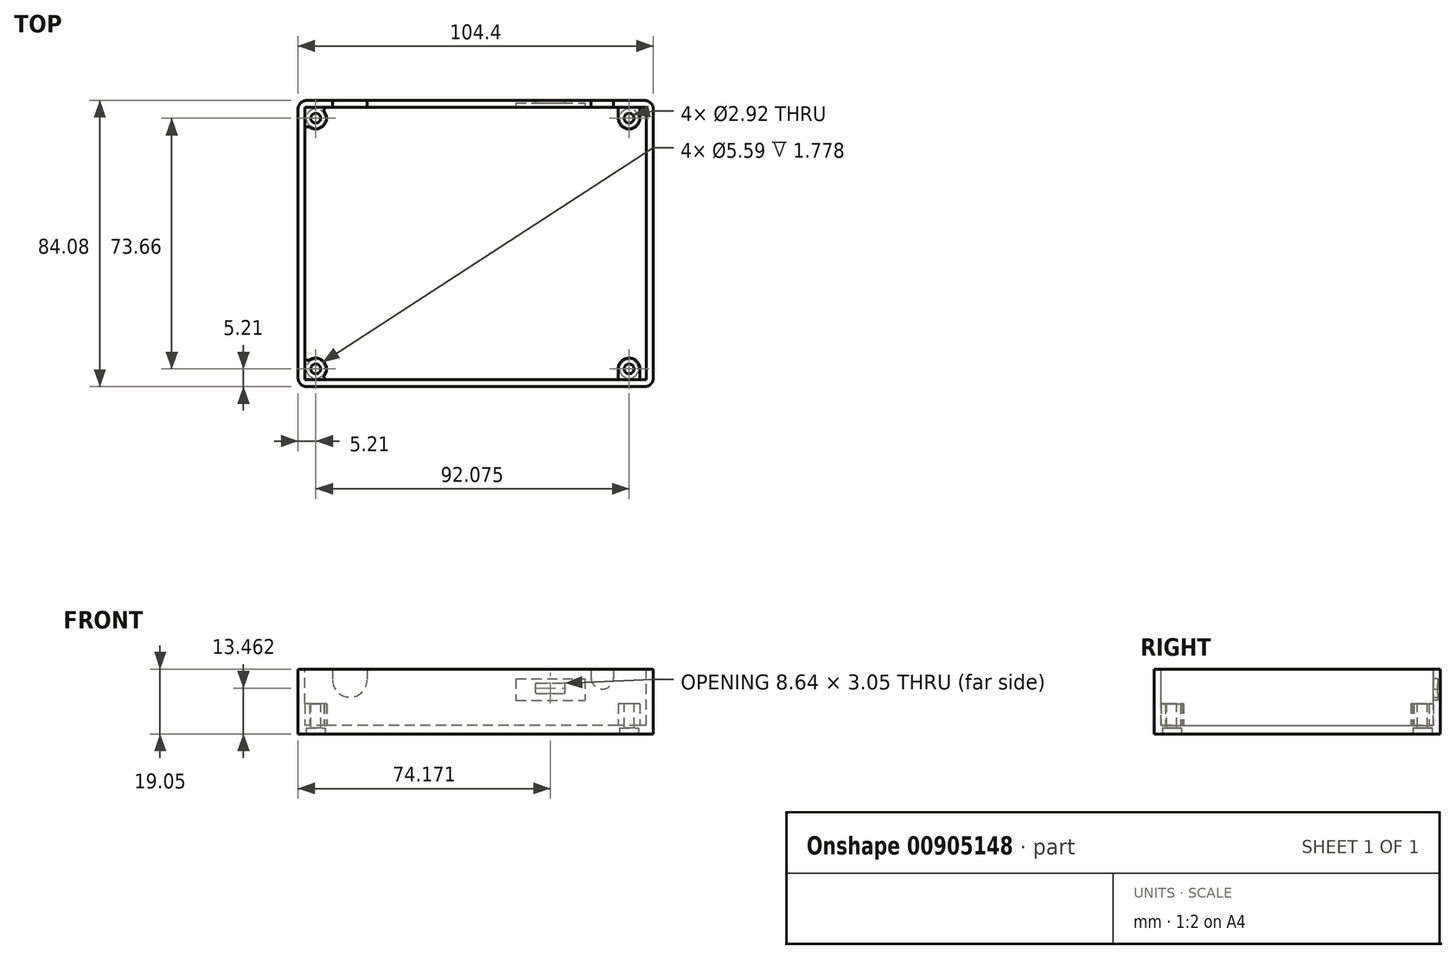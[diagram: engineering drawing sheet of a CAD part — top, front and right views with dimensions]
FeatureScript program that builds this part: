
annotation { "Feature Type Name" : "Feature", "Feature Type Description" : "" }
export const myFeature = defineFeature(function(context is Context, id is Id, definition is map)
    precondition{}
    {
        {
            var Q0;
            Q0=qCreatedBy(makeId("Top.planeOp"),FACE);
            var sketch = newSketch(context, id + "F0", { "sketchPlane" : qUnion([Q0])});
            skLineSegment(sketch, "E0.bottom", {"start": v(52.2, -42.04) * mm, "end": v(-52.2, -42.04) * mm});
            skLineSegment(sketch, "E0.top", {"start": v(52.2, 42.04) * mm, "end": v(-52.2, 42.04) * mm});
            skLineSegment(sketch, "E0.left", {"start": v(52.2, -42.04) * mm, "end": v(52.2, 42.04) * mm});
            skLineSegment(sketch, "E0.right", {"start": v(-52.2, -42.04) * mm, "end": v(-52.2, 42.04) * mm});
            skPoint(sketch, "E0.middle", {"position": v(0, 0) * mm});
            skSolve(sketch);
        }
        {
            var Q0;
            Q0 = qSketchRegion(id + "F0", true);
            extrude(context, id + "F1", {"entities" : qUnion([Q0]), "depth" : 19.05 * mm, "offsetDistance" : 25.4 * mm});
        }
        {
            var Q0;
            Q0=makeQuery(id+"F1.opExtrude","CAP_FACE",FACE,{"disambiguationData":[OSD([sQuery(id+"F0.wireOp",EDGE,"E0.bottom"),sQuery(id+"F0.wireOp",EDGE,"E0.top"),sQuery(id+"F0.wireOp",EDGE,"E0.left"),sQuery(id+"F0.wireOp",EDGE,"E0.right")])],"isStart":false});
            var sketch = newSketch(context, id + "F2", { "sketchPlane" : qUnion([Q0])});
            skLineSegment(sketch, "E1.bottom", {"start": v(50.16, -40) * mm, "end": v(-50.16, -40) * mm});
            skLineSegment(sketch, "E1.top", {"start": v(50.16, 40) * mm, "end": v(-50.16, 40) * mm});
            skLineSegment(sketch, "E1.left", {"start": v(50.16, -40) * mm, "end": v(50.16, 40) * mm});
            skLineSegment(sketch, "E1.right", {"start": v(-50.16, -40) * mm, "end": v(-50.16, 40) * mm});
            skPoint(sketch, "E1.middle", {"position": v(0, 0) * mm});
            skSolve(sketch);
        }
        {
            var Q0;
            Q0=makeQuery(id+"F2.imprint","IMPRINT",FACE,{"disambiguationData":[TD([[makeQuery(id+"F2.imprint","IMPRINT",EDGE,{"derivedFrom":sQuery(id+"F2.wireOp",EDGE,"E1.bottom")}),-1.0]])]});
            extrude(context, id + "F3", {"entities" : qUnion([Q0]), "operationType" : NewBodyOperationType.REMOVE, "oppositeDirection" : true, "depth" : 16.5 * mm, "offsetDistance" : 25.4 * mm});
        }
        {
            var Q0;
            Q0=makeQuery(id+"F1.opExtrude","SWEPT_FACE",FACE,{"disambiguationData":[OSD([sQuery(id+"F0.wireOp",EDGE,"E0.top")])]});
            var sketch = newSketch(context, id + "F4", { "sketchPlane" : qUnion([Q0])});
            skPoint(sketch, "E2", {"position": v(36.96, 15.88) * mm});
            skCircle(sketch, "E3", {"center": v(36.96, 15.88) * mm, "radius": 5.08 * mm});
            skLineSegment(sketch, "E4", {"start": v(36.96, 15.88) * mm, "end": v(31.88, 15.88) * mm, "construction": true});
            skLineSegment(sketch, "E5", {"start": v(36.96, 15.88) * mm, "end": v(42.04, 15.88) * mm, "construction": true});
            skLineSegment(sketch, "E6", {"start": v(31.88, 15.88) * mm, "end": v(31.88, 19.05) * mm});
            skLineSegment(sketch, "E7", {"start": v(42.04, 15.88) * mm, "end": v(42.04, 19.05) * mm});
            skSolve(sketch);
        }
        {
            var Q0;
            Q0 = qSketchRegion(id + "F4", true);
            var Q1;
            {var subQ0=sQuery(id+"F4.wireOp",EDGE,"E7");Q1=makeQuery(id+"F4.imprint","IMPRINT",FACE,{"disambiguationData":[TD([[makeQuery(id+"F4.imprint","IMPRINT",EDGE,{"derivedFrom":subQ0}),1.0]])]});}
            var Q2;
            {var subQ0=sQuery(id+"F4.wireOp",EDGE,"E6");Q2=makeQuery(id+"F4.imprint","IMPRINT",FACE,{"disambiguationData":[TD([[makeQuery(id+"F4.imprint","IMPRINT",EDGE,{"derivedFrom":subQ0}),-1.0]])]});}
            extrude(context, id + "F5", {"entities" : qUnion([Q0, Q1, Q2]), "operationType" : NewBodyOperationType.REMOVE, "endBound" : BoundingType.UP_TO_NEXT, "oppositeDirection" : true, "depth" : 25.4 * mm, "offsetDistance" : 25.4 * mm});
        }
        {
            var Q0;
            Q0=makeQuery(id+"F1.opExtrude","SWEPT_FACE",FACE,{"disambiguationData":[OSD([sQuery(id+"F0.wireOp",EDGE,"E0.top")])]});
            var sketch = newSketch(context, id + "F6", { "sketchPlane" : qUnion([Q0])});
            skPoint(sketch, "E8", {"position": v(-37.21, 16.51) * mm});
            skCircle(sketch, "E9", {"center": v(-37.21, 16.51) * mm, "radius": 3.3 * mm});
            skLineSegment(sketch, "E10", {"start": v(-37.21, 16.51) * mm, "end": v(-40.51, 16.51) * mm, "construction": true});
            skLineSegment(sketch, "E11", {"start": v(-37.21, 16.51) * mm, "end": v(-33.9, 16.51) * mm, "construction": true});
            skLineSegment(sketch, "E12", {"start": v(-40.51, 16.51) * mm, "end": v(-40.51, 19.05) * mm});
            skLineSegment(sketch, "E13", {"start": v(-33.9, 16.51) * mm, "end": v(-33.9, 19.05) * mm});
            skSolve(sketch);
        }
        {
            var Q0;
            {var subQ0=sQuery(id+"F6.wireOp",EDGE,"E12");Q0=makeQuery(id+"F6.imprint","IMPRINT",FACE,{"disambiguationData":[TD([[makeQuery(id+"F6.imprint","IMPRINT",EDGE,{"derivedFrom":subQ0}),-1.0]])]});}
            var Q1;
            {var subQ0=sQuery(id+"F6.wireOp",EDGE,"E9");var subQ1=makeQuery(id+"F6.imprint","INTERSECT",VERTEX,{"derivedFrom":[subQ0,sQuery(id+"F6.wireOp",EDGE,"E12")]});Q1=makeQuery(id+"F6.imprint","IMPRINT",FACE,{"disambiguationData":[TD([[makeQuery(id+"F6.imprint","IMPRINT",EDGE,{"disambiguationData":[TD([[subQ1,1.0]])],"derivedFrom":subQ0}),1.0]])]});}
            var Q2;
            {var subQ0=sQuery(id+"F6.wireOp",EDGE,"E13");Q2=makeQuery(id+"F6.imprint","IMPRINT",FACE,{"disambiguationData":[TD([[makeQuery(id+"F6.imprint","IMPRINT",EDGE,{"derivedFrom":subQ0}),1.0]])]});}
            extrude(context, id + "F7", {"entities" : qUnion([Q0, Q1, Q2]), "operationType" : NewBodyOperationType.REMOVE, "endBound" : BoundingType.UP_TO_NEXT, "oppositeDirection" : true, "depth" : 25.4 * mm, "offsetDistance" : 25.4 * mm});
        }
        {
            var Q0;
            Q0=makeQuery(id+"F1.opExtrude","SWEPT_FACE",FACE,{"disambiguationData":[OSD([sQuery(id+"F0.wireOp",EDGE,"E0.top")])]});
            var sketch = newSketch(context, id + "F8", { "sketchPlane" : qUnion([Q0])});
            skPoint(sketch, "E14", {"position": v(-21.97, 13.46) * mm});
            skLineSegment(sketch, "E15.bottom", {"start": v(-17.9, 11.94) * mm, "end": v(-26.04, 11.94) * mm});
            skLineSegment(sketch, "E15.top", {"start": v(-17.9, 14.99) * mm, "end": v(-26.04, 14.99) * mm});
            skLineSegment(sketch, "E15.left", {"start": v(-17.65, 12.2) * mm, "end": v(-17.65, 14.73) * mm});
            skLineSegment(sketch, "E15.right", {"start": v(-26.29, 12.2) * mm, "end": v(-26.29, 14.73) * mm});
            skArc(sketch, "E16.0", {"start": v(-40.51, 16.51) * mm, "mid": v(-37.21, 13.2) * mm, "end": v(-33.9, 16.51) * mm});
            skPoint(sketch, "E17.visualSharp", {"position": v(-17.65, 14.99) * mm});
            skArc(sketch, "E17.filletArc", {"start": v(-17.65, 14.73) * mm, "mid": v(-17.73, 14.91) * mm, "end": v(-17.9, 14.99) * mm});
            skPoint(sketch, "E18.visualSharp", {"position": v(-17.65, 11.94) * mm});
            skArc(sketch, "E18.filletArc", {"start": v(-17.9, 11.94) * mm, "mid": v(-17.73, 12.01) * mm, "end": v(-17.65, 12.2) * mm});
            skPoint(sketch, "E19.visualSharp", {"position": v(-26.29, 14.99) * mm});
            skArc(sketch, "E19.filletArc", {"start": v(-26.04, 14.99) * mm, "mid": v(-26.21, 14.91) * mm, "end": v(-26.29, 14.73) * mm});
            skPoint(sketch, "E20.visualSharp", {"position": v(-26.29, 11.94) * mm});
            skArc(sketch, "E20.filletArc", {"start": v(-26.29, 12.2) * mm, "mid": v(-26.21, 12.01) * mm, "end": v(-26.04, 11.94) * mm});
            skSolve(sketch);
        }
        {
            var Q0;
            Q0=makeQuery(id+"F8.imprint","IMPRINT",FACE,{"disambiguationData":[TD([[makeQuery(id+"F8.imprint","IMPRINT",EDGE,{"derivedFrom":sQuery(id+"F8.wireOp",EDGE,"E15.bottom")}),-1.0]])]});
            extrude(context, id + "F9", {"entities" : qUnion([Q0]), "operationType" : NewBodyOperationType.REMOVE, "endBound" : BoundingType.UP_TO_NEXT, "oppositeDirection" : true, "depth" : 25.4 * mm, "offsetDistance" : 25.4 * mm});
        }
        {
            var Q0;
            Q0=makeQuery(id+"F1.opExtrude","SWEPT_EDGE",EDGE,{"disambiguationData":[OSD([sQuery(id+"F0.wireOp",EDGE,"E0.top"),sQuery(id+"F0.wireOp",EDGE,"E0.left")])]});
            var Q1;
            Q1=makeQuery(id+"F1.opExtrude","SWEPT_EDGE",EDGE,{"disambiguationData":[OSD([sQuery(id+"F0.wireOp",EDGE,"E0.top"),sQuery(id+"F0.wireOp",EDGE,"E0.right")])]});
            var Q2;
            Q2=makeQuery(id+"F1.opExtrude","SWEPT_EDGE",EDGE,{"disambiguationData":[OSD([sQuery(id+"F0.wireOp",EDGE,"E0.bottom"),sQuery(id+"F0.wireOp",EDGE,"E0.right")])]});
            var Q3;
            Q3=makeQuery(id+"F1.opExtrude","SWEPT_EDGE",EDGE,{"disambiguationData":[OSD([sQuery(id+"F0.wireOp",EDGE,"E0.bottom"),sQuery(id+"F0.wireOp",EDGE,"E0.left")])]});
            fillet(context, id + "F10", {"entities" : qUnion([Q0, Q1, Q2, Q3]), "radius" : 2.54 * mm, "tangentPropagation" : true, "allowEdgeOverflow" : false});
        }
        {
            var Q0;
            Q0=makeQuery(id+"F3.boolean.opBoolean","COPY",FACE,{"derivedFrom":makeQuery(id+"F3.opExtrude","CAP_FACE",FACE,{"disambiguationData":[OSD([sQuery(id+"F2.wireOp",EDGE,"E1.bottom"),sQuery(id+"F2.wireOp",EDGE,"E1.top"),sQuery(id+"F2.wireOp",EDGE,"E1.left"),sQuery(id+"F2.wireOp",EDGE,"E1.right")])],"isStart":false})});
            var sketch = newSketch(context, id + "F11", { "sketchPlane" : qUnion([Q0])});
            skLineSegment(sketch, "E21.bottom", {"start": v(-47, 36.83) * mm, "end": v(45.08, 36.83) * mm, "construction": true});
            skLineSegment(sketch, "E21.top", {"start": v(-46.99, -36.83) * mm, "end": v(45.09, -36.83) * mm, "construction": true});
            skLineSegment(sketch, "E21.left", {"start": v(-47, 36.83) * mm, "end": v(-46.99, -36.83) * mm, "construction": true});
            skLineSegment(sketch, "E21.right", {"start": v(45.08, 36.83) * mm, "end": v(45.09, -36.83) * mm, "construction": true});
            skArc(sketch, "E22", {"start": v(-48.74, 34.18) * mm, "mid": v(-44.66, 34.67) * mm, "end": v(-44.48, 38.78) * mm});
            skArc(sketch, "E23", {"start": v(48.26, -36.83) * mm, "mid": v(45.09, -33.65) * mm, "end": v(41.91, -36.83) * mm});
            skArc(sketch, "E24", {"start": v(41.9, 36.83) * mm, "mid": v(45.12, 33.66) * mm, "end": v(48.26, 36.9) * mm});
            skLineSegment(sketch, "E25", {"start": v(41.9, 36.83) * mm, "end": v(41.9, 40) * mm});
            skLineSegment(sketch, "E26", {"start": v(41.91, -36.83) * mm, "end": v(41.91, -40) * mm});
            skLineSegment(sketch, "E27", {"start": v(48.26, -36.83) * mm, "end": v(48.26, -40) * mm});
            skLineSegment(sketch, "E28", {"start": v(48.26, 36.9) * mm, "end": v(48.2, 40) * mm});
            skArc(sketch, "E29", {"start": v(-43.66, 40) * mm, "mid": v(-44.4, 39.62) * mm, "end": v(-44.48, 38.78) * mm});
            skArc(sketch, "E30", {"start": v(-48.74, 34.18) * mm, "mid": v(-49.7, 34.2) * mm, "end": v(-50.16, 33.34) * mm});
            skArc(sketch, "E31.MirrorCS", {"start": v(-43.66, -40) * mm, "mid": v(-44.4, -39.62) * mm, "end": v(-44.48, -38.78) * mm});
            skArc(sketch, "E32.MirrorCS", {"start": v(-48.74, -34.18) * mm, "mid": v(-49.7, -34.2) * mm, "end": v(-50.16, -33.34) * mm});
            skArc(sketch, "E33", {"start": v(-44.48, -38.78) * mm, "mid": v(-44.66, -34.67) * mm, "end": v(-48.74, -34.18) * mm});
            skSolve(sketch);
        }
        {
            var Q0;
            Q0=makeQuery(id+"F3.boolean.opBoolean","COPY",FACE,{"derivedFrom":makeQuery(id+"F3.opExtrude","SWEPT_FACE",FACE,{"disambiguationData":[OSD([sQuery(id+"F2.wireOp",EDGE,"E1.top")])]})});
            var sketch = newSketch(context, id + "F12", { "sketchPlane" : qUnion([Q0])});
            skLineSegment(sketch, "E34.bottom", {"start": v(11.81, 16.26) * mm, "end": v(32.13, 16.26) * mm});
            skLineSegment(sketch, "E34.top", {"start": v(11.81, 9.9) * mm, "end": v(32.13, 9.9) * mm});
            skLineSegment(sketch, "E34.left", {"start": v(11.81, 16.26) * mm, "end": v(11.81, 9.9) * mm});
            skLineSegment(sketch, "E34.right", {"start": v(32.13, 16.26) * mm, "end": v(32.13, 9.9) * mm});
            skSolve(sketch);
        }
        {
            var Q0;
            Q0 = qSketchRegion(id + "F12", true);
            extrude(context, id + "F13", {"entities" : qUnion([Q0]), "operationType" : NewBodyOperationType.REMOVE, "oppositeDirection" : true, "depth" : 1.27 * mm, "offsetDistance" : 25.4 * mm});
        }
        {
            var Q0;
            {var subQ1=sQuery(id+"F11.wireOp",EDGE,"E22");Q0=makeQuery(id+"F11.imprint","IMPRINT",FACE,{"disambiguationData":[TD([[makeQuery(id+"F11.imprint","IMPRINT",EDGE,{"derivedFrom":subQ1}),1.0]])]});}
            var Q1;
            Q1=makeQuery(id+"F11.imprint","IMPRINT",FACE,{"disambiguationData":[TD([[makeQuery(id+"F11.imprint","IMPRINT",EDGE,{"derivedFrom":sQuery(id+"F11.wireOp",EDGE,"E24")}),1.0]])]});
            var Q2;
            Q2=makeQuery(id+"F11.imprint","IMPRINT",FACE,{"disambiguationData":[TD([[makeQuery(id+"F11.imprint","IMPRINT",EDGE,{"derivedFrom":sQuery(id+"F11.wireOp",EDGE,"E23")}),1.0]])]});
            var Q3;
            {var subQ5=sQuery(id+"F11.wireOp",EDGE,"E33");Q3=makeQuery(id+"F11.imprint","IMPRINT",FACE,{"disambiguationData":[TD([[makeQuery(id+"F11.imprint","IMPRINT",EDGE,{"derivedFrom":subQ5}),1.0]])]});}
            extrude(context, id + "F14", {"entities" : qUnion([Q0, Q1, Q2, Q3]), "operationType" : NewBodyOperationType.ADD, "depth" : 6.35 * mm, "offsetDistance" : 25.4 * mm});
        }
        {
            var Q0;
            Q0=makeQuery(id+"F14.opExtrude","CAP_FACE",FACE,{"disambiguationData":[OSD([sQuery(id+"F2.wireOp",EDGE,"E1.top"),sQuery(id+"F2.wireOp",EDGE,"E1.right"),sQuery(id+"F11.wireOp",EDGE,"E22"),sQuery(id+"F11.wireOp",EDGE,"E29"),sQuery(id+"F11.wireOp",EDGE,"E30")])],"isStart":false});
            var sketch = newSketch(context, id + "F15", { "sketchPlane" : qUnion([Q0])});
            skArc(sketch, "E35.0", {"start": v(-48.74, 34.18) * mm, "mid": v(-44.66, 34.67) * mm, "end": v(-44.48, 38.78) * mm});
            skArc(sketch, "E36.0", {"start": v(41.9, 36.83) * mm, "mid": v(45.12, 33.66) * mm, "end": v(48.26, 36.9) * mm});
            skArc(sketch, "E37.0", {"start": v(48.26, -36.83) * mm, "mid": v(45.09, -33.65) * mm, "end": v(41.91, -36.83) * mm});
            skArc(sketch, "E38.0", {"start": v(-44.48, -38.78) * mm, "mid": v(-44.66, -34.67) * mm, "end": v(-48.74, -34.18) * mm});
            skCircle(sketch, "E39", {"center": v(-47, 36.83) * mm, "radius": 1.46 * mm});
            skCircle(sketch, "E40", {"center": v(45.08, 36.83) * mm, "radius": 1.46 * mm});
            skCircle(sketch, "E41", {"center": v(-46.99, -36.83) * mm, "radius": 1.46 * mm});
            skCircle(sketch, "E42", {"center": v(45.09, -36.83) * mm, "radius": 1.46 * mm});
            skSolve(sketch);
        }
        {
            var Q0;
            Q0=makeQuery(id+"F15.imprint","IMPRINT",FACE,{"disambiguationData":[TD([[makeQuery(id+"F15.imprint","IMPRINT",EDGE,{"derivedFrom":sQuery(id+"F15.wireOp",EDGE,"E40")}),1.0]])]});
            var Q1;
            Q1=makeQuery(id+"F15.imprint","IMPRINT",FACE,{"disambiguationData":[TD([[makeQuery(id+"F15.imprint","IMPRINT",EDGE,{"derivedFrom":sQuery(id+"F15.wireOp",EDGE,"E39")}),1.0]])]});
            var Q2;
            Q2=makeQuery(id+"F15.imprint","IMPRINT",FACE,{"disambiguationData":[TD([[makeQuery(id+"F15.imprint","IMPRINT",EDGE,{"derivedFrom":sQuery(id+"F15.wireOp",EDGE,"E41")}),1.0]])]});
            var Q3;
            Q3=makeQuery(id+"F15.imprint","IMPRINT",FACE,{"disambiguationData":[TD([[makeQuery(id+"F15.imprint","IMPRINT",EDGE,{"derivedFrom":sQuery(id+"F15.wireOp",EDGE,"E42")}),1.0]])]});
            extrude(context, id + "F16", {"entities" : qUnion([Q0, Q1, Q2, Q3]), "operationType" : NewBodyOperationType.REMOVE, "oppositeDirection" : true, "depth" : 25.4 * mm, "offsetDistance" : 25.4 * mm});
        }
        {
            var Q0;
            Q0=makeQuery(id+"F1.opExtrude","CAP_FACE",FACE,{"disambiguationData":[OSD([sQuery(id+"F0.wireOp",EDGE,"E0.bottom"),sQuery(id+"F0.wireOp",EDGE,"E0.top"),sQuery(id+"F0.wireOp",EDGE,"E0.left"),sQuery(id+"F0.wireOp",EDGE,"E0.right")])],"isStart":true});
            var sketch = newSketch(context, id + "F17", { "sketchPlane" : qUnion([Q0])});
            skCircle(sketch, "E43", {"center": v(-46.99, 36.83) * mm, "radius": 2.8 * mm});
            skCircle(sketch, "E44", {"center": v(45.09, 36.83) * mm, "radius": 2.8 * mm});
            skCircle(sketch, "E45", {"center": v(45.08, -36.83) * mm, "radius": 2.8 * mm});
            skCircle(sketch, "E46", {"center": v(-47, -36.83) * mm, "radius": 2.8 * mm});
            skSolve(sketch);
        }
        {
            var Q0;
            Q0=makeQuery(id+"F17.imprint","IMPRINT",FACE,{"disambiguationData":[TD([[makeQuery(id+"F17.imprint","IMPRINT",EDGE,{"derivedFrom":sQuery(id+"F17.wireOp",EDGE,"E44")}),1.0]])]});
            var Q1;
            Q1=makeQuery(id+"F17.imprint","IMPRINT",FACE,{"disambiguationData":[TD([[makeQuery(id+"F17.imprint","IMPRINT",EDGE,{"derivedFrom":sQuery(id+"F17.wireOp",EDGE,"E45")}),1.0]])]});
            var Q2;
            Q2=makeQuery(id+"F17.imprint","IMPRINT",FACE,{"disambiguationData":[TD([[makeQuery(id+"F17.imprint","IMPRINT",EDGE,{"derivedFrom":sQuery(id+"F17.wireOp",EDGE,"E46")}),1.0]])]});
            var Q3;
            Q3=makeQuery(id+"F17.imprint","IMPRINT",FACE,{"disambiguationData":[TD([[makeQuery(id+"F17.imprint","IMPRINT",EDGE,{"derivedFrom":sQuery(id+"F17.wireOp",EDGE,"E43")}),1.0]])]});
            extrude(context, id + "F18", {"entities" : qUnion([Q0, Q1, Q2, Q3]), "operationType" : NewBodyOperationType.REMOVE, "oppositeDirection" : true, "depth" : 1.78 * mm, "offsetDistance" : 25.4 * mm});
        }
    });
